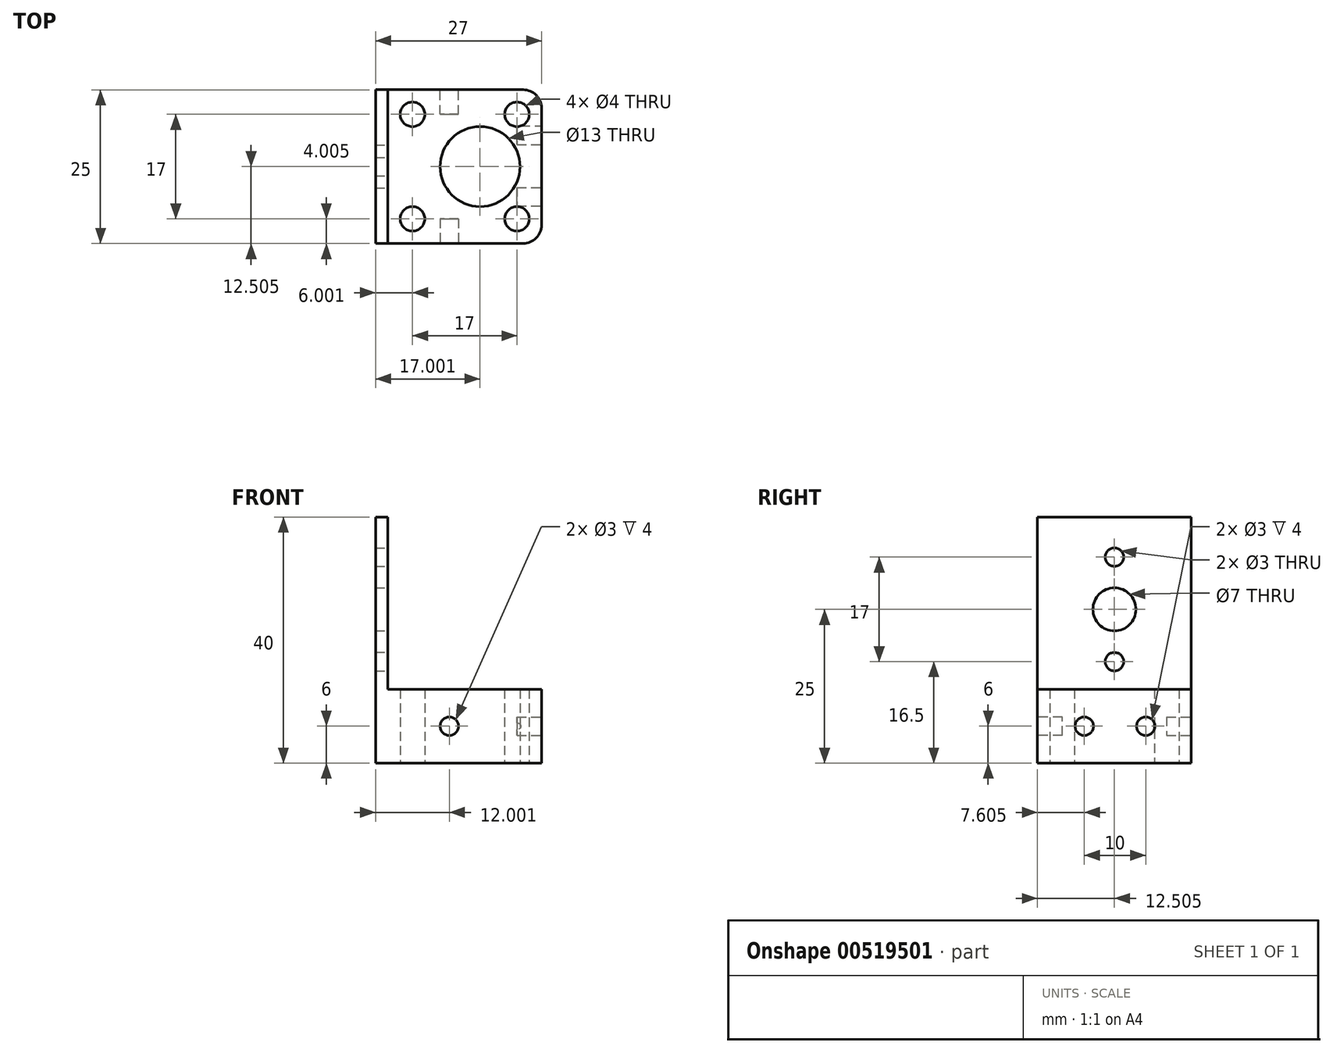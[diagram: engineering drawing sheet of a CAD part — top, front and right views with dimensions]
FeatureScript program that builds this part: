
annotation { "Feature Type Name" : "Feature", "Feature Type Description" : "" }
export const myFeature = defineFeature(function(context is Context, id is Id, definition is map)
    precondition{}
    {
        {
            var Q0;
            Q0=qCreatedBy(makeId("Top.planeOp"),FACE);
            var sketch = newSketch(context, id + "F0", { "sketchPlane" : qUnion([Q0])});
            skLineSegment(sketch, "E0.bottom", {"start": v(-13.07, 7.4) * mm, "end": v(13.93, 7.4) * mm});
            skLineSegment(sketch, "E0.top", {"start": v(-13.07, -17.6) * mm, "end": v(13.93, -17.6) * mm});
            skLineSegment(sketch, "E0.left", {"start": v(-13.07, 7.4) * mm, "end": v(-13.07, -17.6) * mm});
            skLineSegment(sketch, "E0.right", {"start": v(13.93, 7.4) * mm, "end": v(13.93, -17.6) * mm});
            skPoint(sketch, "E1", {"position": v(-7.07, 3.4) * mm});
            skPoint(sketch, "E2", {"position": v(9.93, 3.4) * mm});
            skPoint(sketch, "E3", {"position": v(9.93, -13.6) * mm});
            skPoint(sketch, "E4", {"position": v(-7.07, -13.6) * mm});
            skPoint(sketch, "E5", {"position": v(3.93, -5.1) * mm});
            skCircle(sketch, "E6", {"center": v(3.93, -5.1) * mm, "radius": 6.5 * mm});
            skCircle(sketch, "E7", {"center": v(-7.07, 3.4) * mm, "radius": 2 * mm});
            skCircle(sketch, "E8", {"center": v(-7.07, -13.6) * mm, "radius": 2 * mm});
            skCircle(sketch, "E9", {"center": v(9.93, -13.6) * mm, "radius": 2 * mm});
            skCircle(sketch, "E10", {"center": v(9.93, 3.4) * mm, "radius": 2 * mm});
            skSolve(sketch);
        }
        {
            var Q0;
            Q0=makeQuery(id+"F0.imprint","IMPRINT",FACE,{"disambiguationData":[TD([[makeQuery(id+"F0.imprint","IMPRINT",EDGE,{"derivedFrom":sQuery(id+"F0.wireOp",EDGE,"E0.bottom")}),-1.0]])]});
            extrude(context, id + "F1", {"entities" : qUnion([Q0]), "depth" : 12 * mm, "offsetDistance" : 25 * mm});
        }
        {
            var Q0;
            Q0=makeQuery(id+"F1.opExtrude","CAP_FACE",FACE,{"disambiguationData":[OSD([sQuery(id+"F0.wireOp",EDGE,"E0.bottom"),sQuery(id+"F0.wireOp",EDGE,"E0.top"),sQuery(id+"F0.wireOp",EDGE,"E0.left"),sQuery(id+"F0.wireOp",EDGE,"E0.right"),sQuery(id+"F0.wireOp",EDGE,"E6"),sQuery(id+"F0.wireOp",EDGE,"E7"),sQuery(id+"F0.wireOp",EDGE,"E8"),sQuery(id+"F0.wireOp",EDGE,"E9"),sQuery(id+"F0.wireOp",EDGE,"E10")])],"isStart":false});
            var sketch = newSketch(context, id + "F2", { "sketchPlane" : qUnion([Q0])});
            skLineSegment(sketch, "E11.bottom", {"start": v(-13.07, 7.4) * mm, "end": v(-11.07, 7.4) * mm});
            skLineSegment(sketch, "E11.top", {"start": v(-13.07, -17.6) * mm, "end": v(-11.07, -17.6) * mm});
            skLineSegment(sketch, "E11.left", {"start": v(-13.07, 7.4) * mm, "end": v(-13.07, -17.6) * mm});
            skLineSegment(sketch, "E11.right", {"start": v(-11.07, 7.4) * mm, "end": v(-11.07, -17.6) * mm});
            skSolve(sketch);
        }
        {
            var Q0;
            Q0=makeQuery(id+"F2.imprint","IMPRINT",FACE,{"disambiguationData":[TD([[makeQuery(id+"F2.imprint","IMPRINT",EDGE,{"derivedFrom":sQuery(id+"F2.wireOp",EDGE,"E11.bottom")}),-1.0]])]});
            extrude(context, id + "F3", {"entities" : qUnion([Q0]), "operationType" : NewBodyOperationType.ADD, "depth" : 28 * mm, "offsetDistance" : 25 * mm});
        }
        {
            var Q0;
            Q0=makeQuery(id+"F1.opExtrude","SWEPT_FACE",FACE,{"disambiguationData":[OSD([sQuery(id+"F0.wireOp",EDGE,"E0.right")])]});
            var sketch = newSketch(context, id + "F4", { "sketchPlane" : qUnion([Q0])});
            skPoint(sketch, "E12", {"position": v(-10, 6) * mm});
            skPoint(sketch, "E13", {"position": v(0, 6) * mm});
            skCircle(sketch, "E14", {"center": v(-10, 6) * mm, "radius": 1.5 * mm});
            skCircle(sketch, "E15", {"center": v(0, 6) * mm, "radius": 1.5 * mm});
            skSolve(sketch);
        }
        {
            var Q0;
            Q0=makeQuery(id+"F4.imprint","IMPRINT",FACE,{"disambiguationData":[TD([[makeQuery(id+"F4.imprint","IMPRINT",EDGE,{"derivedFrom":sQuery(id+"F4.wireOp",EDGE,"E14")}),1.0]])]});
            var Q1;
            Q1=makeQuery(id+"F4.imprint","IMPRINT",FACE,{"disambiguationData":[TD([[makeQuery(id+"F4.imprint","IMPRINT",EDGE,{"derivedFrom":sQuery(id+"F4.wireOp",EDGE,"E15")}),1.0]])]});
            extrude(context, id + "F5", {"entities" : qUnion([Q0, Q1]), "operationType" : NewBodyOperationType.REMOVE, "oppositeDirection" : true, "depth" : 4 * mm, "offsetDistance" : 25 * mm});
        }
        {
            var Q0;
            Q0=makeQuery(id+"F3.boolean.opBoolean","MERGE",FACE,{"derivedFrom":[makeQuery(id+"F1.opExtrude","SWEPT_FACE",FACE,{"disambiguationData":[OSD([sQuery(id+"F0.wireOp",EDGE,"E0.top")])]}),makeQuery(id+"F3.opExtrude","SWEPT_FACE",FACE,{"disambiguationData":[OSD([sQuery(id+"F2.wireOp",EDGE,"E11.top")])]})]});
            var sketch = newSketch(context, id + "F6", { "sketchPlane" : qUnion([Q0])});
            skCircle(sketch, "E16", {"center": v(-1.07, 6) * mm, "radius": 1.5 * mm});
            skSolve(sketch);
        }
        {
            var Q0;
            Q0=makeQuery(id+"F6.imprint","IMPRINT",FACE,{"disambiguationData":[TD([[makeQuery(id+"F6.imprint","IMPRINT",EDGE,{"derivedFrom":sQuery(id+"F6.wireOp",EDGE,"E16")}),1.0]])]});
            var Q1;
            Q1=sQuery(id+"F6.wireOp",EDGE,"E16");
            extrude(context, id + "F7", {"entities" : qUnion([Q0]), "operationType" : NewBodyOperationType.REMOVE, "surfaceEntities" : qUnion([Q1]), "oppositeDirection" : true, "depth" : 4 * mm, "offsetDistance" : 25 * mm});
        }
        {
            var Q0;
            Q0=makeQuery(id+"F3.boolean.opBoolean","MERGE",FACE,{"derivedFrom":[makeQuery(id+"F1.opExtrude","SWEPT_FACE",FACE,{"disambiguationData":[OSD([sQuery(id+"F0.wireOp",EDGE,"E0.bottom")])]}),makeQuery(id+"F3.opExtrude","SWEPT_FACE",FACE,{"disambiguationData":[OSD([sQuery(id+"F2.wireOp",EDGE,"E11.bottom")])]})]});
            var sketch = newSketch(context, id + "F8", { "sketchPlane" : qUnion([Q0])});
            skCircle(sketch, "E17", {"center": v(1.07, 6) * mm, "radius": 1.5 * mm});
            skSolve(sketch);
        }
        {
            var Q0;
            Q0=makeQuery(id+"F8.imprint","IMPRINT",FACE,{"disambiguationData":[TD([[makeQuery(id+"F8.imprint","IMPRINT",EDGE,{"derivedFrom":sQuery(id+"F8.wireOp",EDGE,"E17")}),1.0]])]});
            extrude(context, id + "F9", {"entities" : qUnion([Q0]), "operationType" : NewBodyOperationType.REMOVE, "oppositeDirection" : true, "depth" : 4 * mm, "offsetDistance" : 25 * mm});
        }
        {
            var Q0;
            Q0=makeQuery(id+"F1.opExtrude","SWEPT_EDGE",EDGE,{"disambiguationData":[OSD([sQuery(id+"F0.wireOp",EDGE,"E0.top"),sQuery(id+"F0.wireOp",EDGE,"E0.right")])]});
            var Q1;
            Q1=makeQuery(id+"F1.opExtrude","SWEPT_EDGE",EDGE,{"disambiguationData":[OSD([sQuery(id+"F0.wireOp",EDGE,"E0.bottom"),sQuery(id+"F0.wireOp",EDGE,"E0.right")])]});
            fillet(context, id + "F10", {"entities" : qUnion([Q0, Q1]), "radius" : 3 * mm, "tangentPropagation" : true, "allowEdgeOverflow" : false});
        }
        {
            var Q0;
            Q0=makeQuery(id+"F3.opExtrude","SWEPT_FACE",FACE,{"disambiguationData":[OSD([sQuery(id+"F2.wireOp",EDGE,"E11.right")])]});
            var sketch = newSketch(context, id + "F11", { "sketchPlane" : qUnion([Q0])});
            skCircle(sketch, "E18", {"center": v(-5.1, 33.5) * mm, "radius": 1.5 * mm});
            skCircle(sketch, "E19", {"center": v(-5.1, 25) * mm, "radius": 3.5 * mm});
            skCircle(sketch, "E20", {"center": v(-5.1, 16.5) * mm, "radius": 1.5 * mm});
            skLineSegment(sketch, "E21", {"start": v(-5.1, 33.5) * mm, "end": v(-5.1, -13.51) * mm, "construction": true});
            skSolve(sketch);
        }
        {
            var Q0;
            Q0=makeQuery(id+"F11.imprint","IMPRINT",FACE,{"disambiguationData":[TD([[makeQuery(id+"F11.imprint","IMPRINT",EDGE,{"derivedFrom":sQuery(id+"F11.wireOp",EDGE,"E19")}),1.0]])]});
            var Q1;
            Q1=makeQuery(id+"F11.imprint","IMPRINT",FACE,{"disambiguationData":[TD([[makeQuery(id+"F11.imprint","IMPRINT",EDGE,{"derivedFrom":sQuery(id+"F11.wireOp",EDGE,"E18")}),1.0]])]});
            var Q2;
            Q2=makeQuery(id+"F11.imprint","IMPRINT",FACE,{"disambiguationData":[TD([[makeQuery(id+"F11.imprint","IMPRINT",EDGE,{"derivedFrom":sQuery(id+"F11.wireOp",EDGE,"E20")}),1.0]])]});
            extrude(context, id + "F12", {"entities" : qUnion([Q0, Q1, Q2]), "operationType" : NewBodyOperationType.REMOVE, "oppositeDirection" : true, "depth" : 25 * mm, "offsetDistance" : 25 * mm, "hasSecondDirection" : true, "secondDirectionOppositeDirection" : false, "secondDirectionDepth" : 25 * mm});
        }
    });
